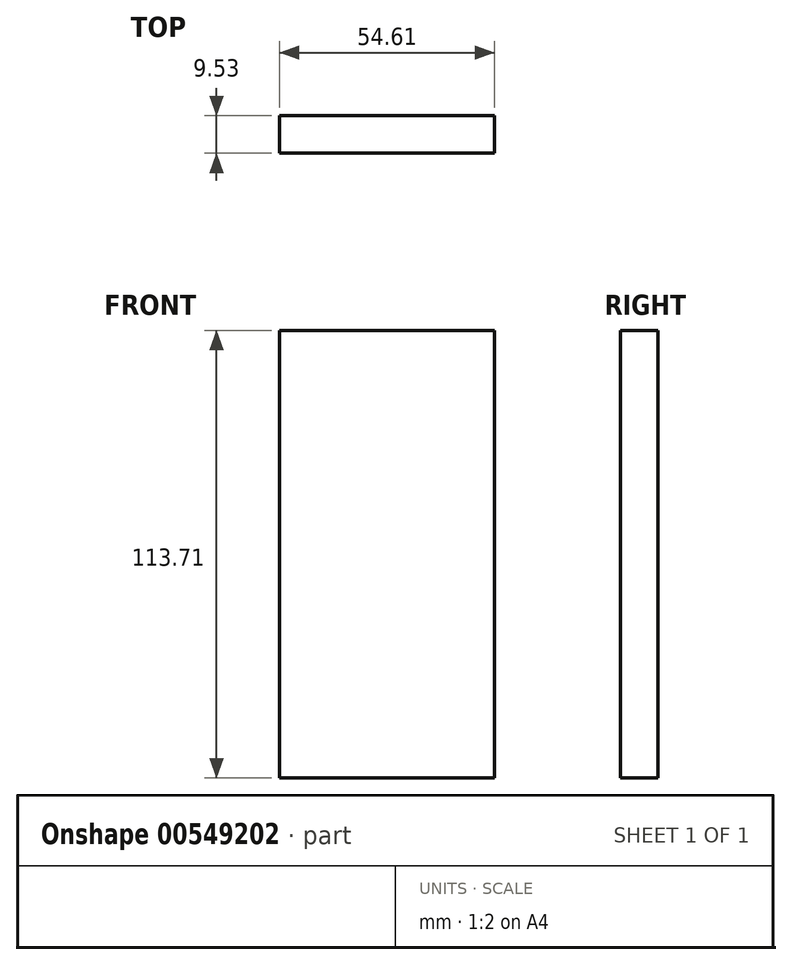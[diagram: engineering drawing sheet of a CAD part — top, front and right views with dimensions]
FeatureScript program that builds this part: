
annotation { "Feature Type Name" : "Feature", "Feature Type Description" : "" }
export const myFeature = defineFeature(function(context is Context, id is Id, definition is map)
    precondition{}
    {
        {
            var Q0;
            Q0=qCreatedBy(makeId("Front.planeOp"),FACE);
            var sketch = newSketch(context, id + "F0", { "sketchPlane" : qUnion([Q0])});
            skLineSegment(sketch, "E0.bottom", {"start": v(-54.6, 54.2) * mm, "end": v(0, 54.2) * mm});
            skLineSegment(sketch, "E0.top", {"start": v(-54.6, -59.52) * mm, "end": v(0, -59.52) * mm});
            skLineSegment(sketch, "E0.left", {"start": v(-54.6, 54.2) * mm, "end": v(-54.6, -59.52) * mm});
            skLineSegment(sketch, "E0.right", {"start": v(0, 54.2) * mm, "end": v(0, -59.52) * mm});
            skSolve(sketch);
        }
        {
            var Q0;
            Q0 = qSketchRegion(id + "F0", true);
            extrude(context, id + "F1", {"entities" : qUnion([Q0]), "depth" : 9.52 * mm, "offsetDistance" : 25.4 * mm});
        }
    });
